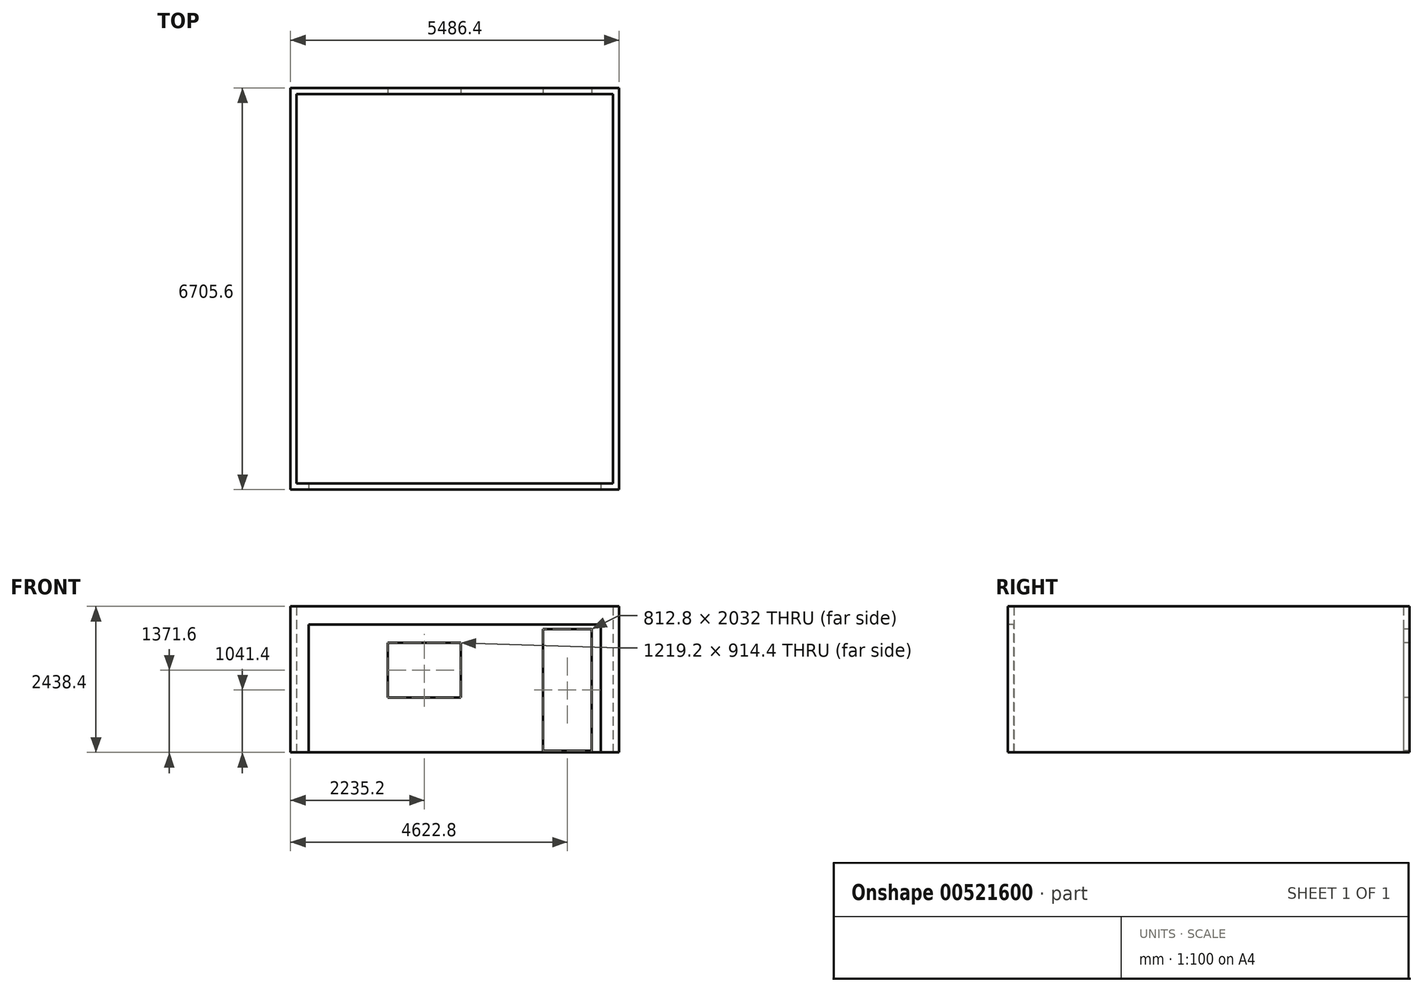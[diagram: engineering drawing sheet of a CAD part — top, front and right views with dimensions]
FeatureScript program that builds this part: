
annotation { "Feature Type Name" : "Feature", "Feature Type Description" : "" }
export const myFeature = defineFeature(function(context is Context, id is Id, definition is map)
    precondition{}
    {
        {
            var Q0;
            Q0=qCreatedBy(makeId("Top.planeOp"),FACE);
            var sketch = newSketch(context, id + "F0", { "sketchPlane" : qUnion([Q0])});
            skLineSegment(sketch, "E0.bottom", {"start": v(2743.2, 3352.8) * mm, "end": v(-2743.2, 3352.8) * mm});
            skLineSegment(sketch, "E0.top", {"start": v(2743.2, -3352.8) * mm, "end": v(-2743.2, -3352.8) * mm});
            skLineSegment(sketch, "E0.left", {"start": v(2743.2, 3352.8) * mm, "end": v(2743.2, -3352.8) * mm});
            skLineSegment(sketch, "E0.right", {"start": v(-2743.2, 3352.8) * mm, "end": v(-2743.2, -3352.8) * mm});
            skPoint(sketch, "E0.middle", {"position": v(0, 0) * mm});
            skLineSegment(sketch, "E1.bottom", {"start": v(2641.6, 3251.2) * mm, "end": v(-2641.6, 3251.2) * mm});
            skLineSegment(sketch, "E1.top", {"start": v(2641.6, -3251.2) * mm, "end": v(-2641.6, -3251.2) * mm});
            skLineSegment(sketch, "E1.left", {"start": v(2641.6, 3251.2) * mm, "end": v(2641.6, -3251.2) * mm});
            skLineSegment(sketch, "E1.right", {"start": v(-2641.6, 3251.2) * mm, "end": v(-2641.6, -3251.2) * mm});
            skSolve(sketch);
        }
        {
            var Q0;
            Q0=qSketchRegion(id+"F0",true);
            extrude(context, id + "F1", {"entities" : qUnion([Q0]), "depth" : 2438.4 * mm});
        }
        {
            var Q0;
            Q0=makeQuery(id+"F1.opExtrude","SWEPT_FACE",FACE,{"disambiguationData":[OSD([sQuery(id+"F0.wireOp",EDGE,"E1.bottom")])]});
            var sketch = newSketch(context, id + "F2", { "sketchPlane" : qUnion([Q0])});
            skLineSegment(sketch, "E2.bottom", {"start": v(101.6, 1828.8) * mm, "end": v(-1117.6, 1828.8) * mm});
            skLineSegment(sketch, "E2.top", {"start": v(101.6, 914.4) * mm, "end": v(-1117.6, 914.4) * mm});
            skLineSegment(sketch, "E2.left", {"start": v(101.6, 1828.8) * mm, "end": v(101.6, 914.4) * mm});
            skLineSegment(sketch, "E2.right", {"start": v(-1117.6, 1828.8) * mm, "end": v(-1117.6, 914.4) * mm});
            skPoint(sketch, "E2.middle", {"position": v(-508, 1371.6) * mm});
            skSolve(sketch);
        }
        {
            var Q0;
            Q0=qSketchRegion(id+"F2",true);
            extrude(context, id + "F3", {"entities" : qUnion([Q0]), "operationType" : NewBodyOperationType.REMOVE, "endBound" : BoundingType.UP_TO_NEXT, "oppositeDirection" : true, "depth" : 25.4 * mm});
        }
        {
            var Q0;
            Q0=makeQuery(id+"F1.opExtrude","SWEPT_FACE",FACE,{"disambiguationData":[OSD([sQuery(id+"F0.wireOp",EDGE,"E1.bottom")])]});
            var sketch = newSketch(context, id + "F4", { "sketchPlane" : qUnion([Q0])});
            skLineSegment(sketch, "E3.bottom", {"start": v(1473.2, 2057.4) * mm, "end": v(2286, 2057.4) * mm});
            skLineSegment(sketch, "E3.top", {"start": v(1473.2, 25.4) * mm, "end": v(2286, 25.4) * mm});
            skLineSegment(sketch, "E3.left", {"start": v(1473.2, 2057.4) * mm, "end": v(1473.2, 25.4) * mm});
            skLineSegment(sketch, "E3.right", {"start": v(2286, 2057.4) * mm, "end": v(2286, 25.4) * mm});
            skPoint(sketch, "E3.middle", {"position": v(1879.6, 1041.4) * mm});
            skSolve(sketch);
        }
        {
            var Q0;
            Q0=qSketchRegion(id+"F4",true);
            extrude(context, id + "F5", {"entities" : qUnion([Q0]), "operationType" : NewBodyOperationType.REMOVE, "endBound" : BoundingType.UP_TO_NEXT, "oppositeDirection" : true, "depth" : 25.4 * mm});
        }
        {
            var Q0;
            Q0=makeQuery(id+"F1.opExtrude","SWEPT_FACE",FACE,{"disambiguationData":[OSD([sQuery(id+"F0.wireOp",EDGE,"E0.top")])]});
            var sketch = newSketch(context, id + "F6", { "sketchPlane" : qUnion([Q0])});
            skLineSegment(sketch, "E4.bottom", {"start": v(2438.4, 2133.6) * mm, "end": v(-2438.4, 2133.6) * mm});
            skLineSegment(sketch, "E4.top", {"start": v(2438.4, 0) * mm, "end": v(-2438.4, 0) * mm});
            skLineSegment(sketch, "E4.left", {"start": v(2438.4, 2133.6) * mm, "end": v(2438.4, 0) * mm});
            skLineSegment(sketch, "E4.right", {"start": v(-2438.4, 2133.6) * mm, "end": v(-2438.4, 0) * mm});
            skPoint(sketch, "E4.middle", {"position": v(0, 1066.8) * mm});
            skLineSegment(sketch, "E5", {"start": v(0, 1066.8) * mm, "end": v(0, 0) * mm, "construction": true});
            skSolve(sketch);
        }
        {
            var Q0;
            Q0=makeQuery(id+"F6.imprint","IMPRINT",FACE,{"disambiguationData":[TD([[makeQuery(id+"F6.imprint","IMPRINT",EDGE,{"derivedFrom":sQuery(id+"F6.wireOp",EDGE,"E4.bottom")}),1.0]])]});
            extrude(context, id + "F7", {"entities" : qUnion([Q0]), "operationType" : NewBodyOperationType.REMOVE, "endBound" : BoundingType.UP_TO_NEXT, "oppositeDirection" : true, "depth" : 25.4 * mm});
        }
    });
